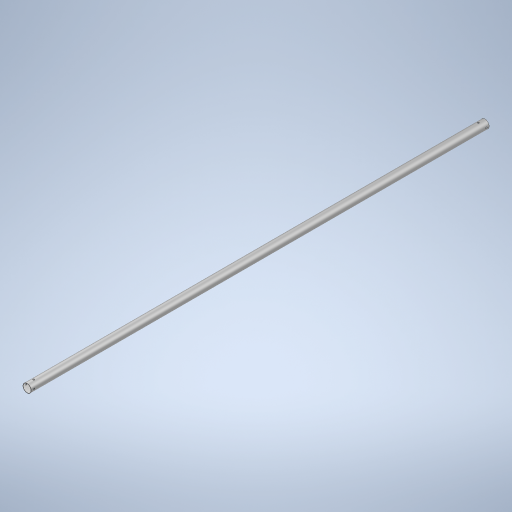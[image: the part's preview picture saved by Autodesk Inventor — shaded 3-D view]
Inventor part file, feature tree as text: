
AUTODESK INVENTOR PART (.ipt)
format: ipt  version: 2024 (Build 280153000, 153)  size: 281,600 bytes
history: native  units: in
note: dims shown in document units (in); Inventor stores cm internally (conversion verified against a paired STEP export)
features: sketch x4, extrude x3, plane x2, other x1
ambient origin geometry x8: Origin, YZ Plane, XZ Plane, XY Plane, X Axis, Y Axis, Z Axis, Center Point
bodies: Solid1 (feature_tree)
feature tree (10):
  sketch  "Sketch1"  dims[d0=2.9961in d1=2.7441in]
  extrude  "Extrusion1"  Depth=2.7441in
  extrude  "Extrusion2"  TaperAngle=0.0deg  [1 undecoded]
  extrude  "Extrusion3"  Depth=0.9843in
  plane  "Work Plane1"
  plane  "Work Plane2"
  sketch  "Sketch2"  dims[d2=163.3858in d3=0.0in]
  sketch  "Sketch3"  dims[d5=3.937in d6=0.0in d7=0.9843in]
  sketch  "Sketch4"  dims[d8=0.5512in d9=2.3622in d10=3.937in d11=0.0in d12=1.187in d13=-1.187in]
  other  "Finish1"
note: 1 required parameter value undecoded (feature->parameter linkage not recoverable at this tier; creation-order binding heuristic only, values carry confidence <= 0.55)
